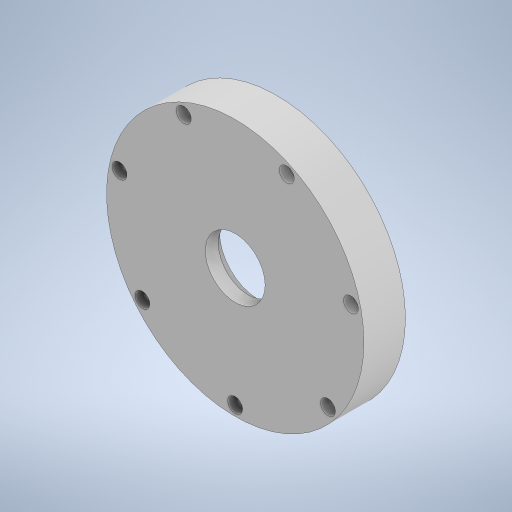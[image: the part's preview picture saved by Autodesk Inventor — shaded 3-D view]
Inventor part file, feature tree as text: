
AUTODESK INVENTOR PART (.ipt)
format: ipt  version: 2023 (Build 270158000, 158)  size: 316,928 bytes
history: native  units: in
note: dims shown in document units (in); Inventor stores cm internally (conversion verified against a paired STEP export)
features: sketch x7, extrude x6, pattern_circular x1
ambient origin geometry x8: Origin, YZ Plane, XZ Plane, XY Plane, X Axis, Y Axis, Z Axis, Center Point
bodies: Solid1 (feature_tree)
feature tree (14):
  extrude  "Extrusion1"  Depth=0.9843in TaperAngle=0.0deg
  extrude  "Extrusion2"  Depth=4.7244in
  extrude  "Extrusion3"  Depth=0.1181in TaperAngle=0.0deg
  extrude  "Extrusion4"  TaperAngle=0.0deg  [1 undecoded]
  pattern_circular  "Circular Pattern1"  [2 undecoded]
  extrude  "Extrusion5"  Depth=0.2441in TaperAngle=360.0deg
  extrude  "Extrusion6"  Depth=0.2441in
  sketch  "Sketch1"  dims[d0=6.1024in d1=0.9843in d2=0.0in]
  sketch  "Sketch2"  dims[d3=0.2362in d4=4.7244in]
  sketch  "Sketch3"  dims[d5=8.2677in d7=360.0deg d9=0.1181in d10=0.0in]
  sketch  "Sketch4"  dims[d11=1.4173in d12=0.0in d13=0.0in]
  sketch  "Sketch5"  dims[d14=3.622in]
  sketch  "Sketch6"  dims[d15=0.4331in d16=0.0in]
  sketch  "Sketch7"  dims[d17=0.2362in d18=0.2362in d19=0.3543in d20=0.2165in d21=90.0deg d22=0.2362in d23=0.0in d24=5.6299in d25=2.7559in d26=360.0deg d28=5.1181in d29=0.0394in d30=0.0in d31=1.8504in d32=0.2441in d33=0.0in]
note: 3 required parameter values undecoded (feature->parameter linkage not recoverable at this tier; creation-order binding heuristic only, values carry confidence <= 0.55)
